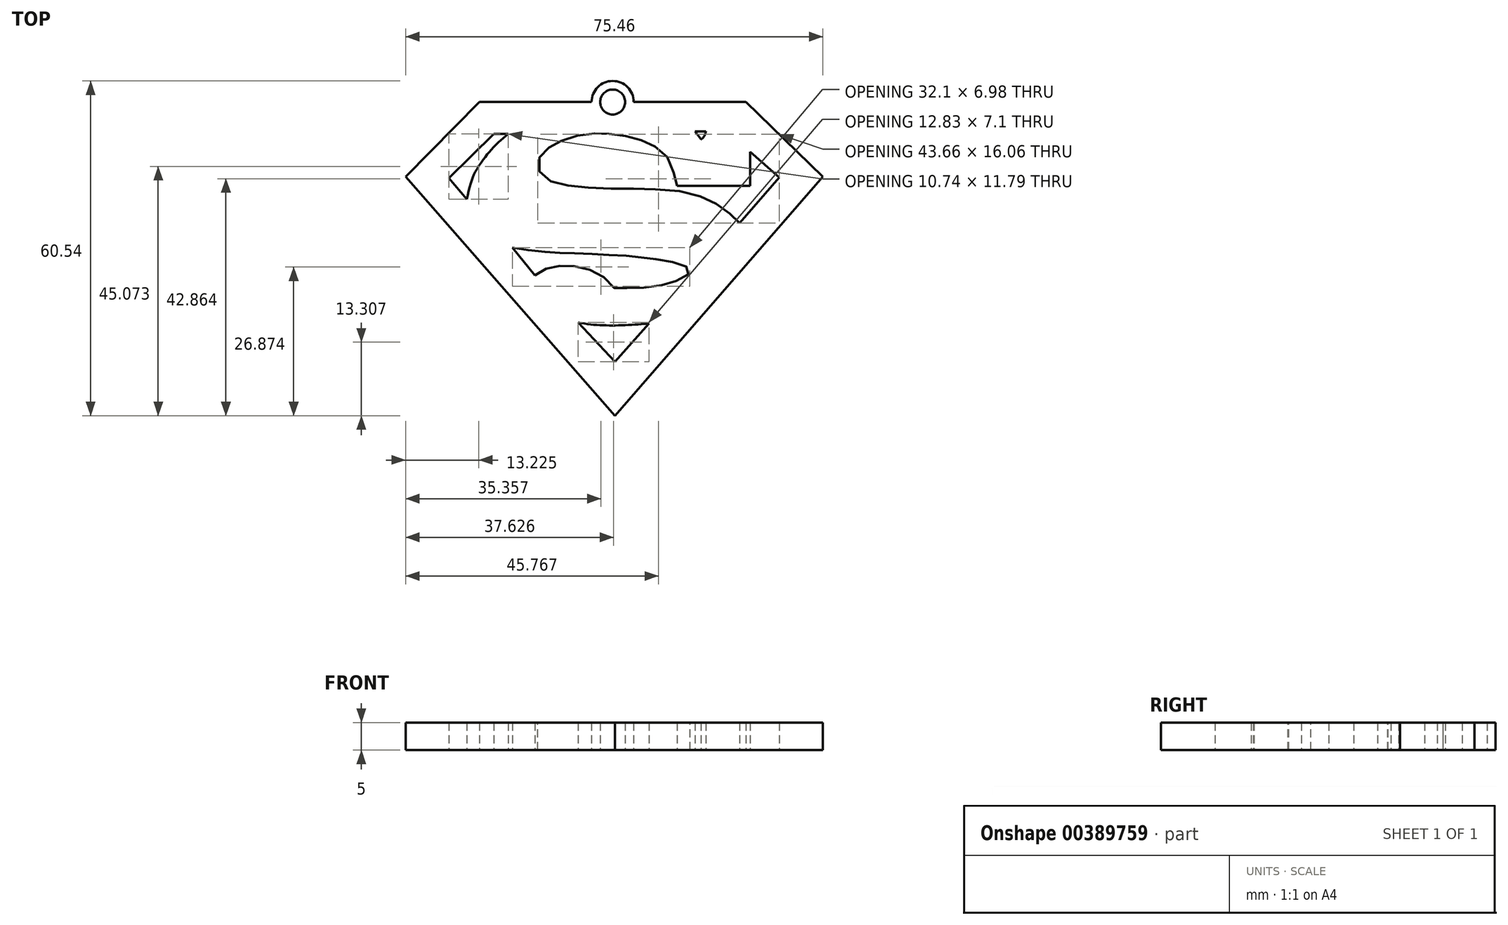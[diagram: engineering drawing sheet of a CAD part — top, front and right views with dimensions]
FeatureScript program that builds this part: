
annotation { "Feature Type Name" : "Feature", "Feature Type Description" : "" }
export const myFeature = defineFeature(function(context is Context, id is Id, definition is map)
    precondition{}
    {
        {
            var Q0;
            Q0=qCreatedBy(makeId("Top.planeOp"),FACE);
            var sketch = newSketch(context, id + "F0", { "sketchPlane" : qUnion([Q0])});
            skLineSegment(sketch, "E0", {"start": v(24.95, 26.24) * mm, "end": v(26.93, 26.24) * mm});
            skLineSegment(sketch, "E1", {"start": v(24.95, 26.24) * mm, "end": v(26.03, 24.83) * mm});
            skFitSpline(sketch, "E2", {"points": [v(26.03, 24.83) * mm, v(26.93, 26.24) * mm], "startDerivative": vector(0.95, 0.22) * mm, "endDerivative": vector(0.66, 2.5) * mm});
            skLineSegment(sketch, "E3", {"start": v(-14.03, 31.56) * mm, "end": v(6.24, 31.56) * mm});
            skLineSegment(sketch, "E4", {"start": v(34.12, 31.56) * mm, "end": v(48.05, 18.07) * mm});
            skLineSegment(sketch, "E5", {"start": v(48.05, 18.07) * mm, "end": v(10.44, -25.17) * mm});
            skLineSegment(sketch, "E6", {"start": v(10.44, -25.17) * mm, "end": v(-27.41, 18.07) * mm});
            skLineSegment(sketch, "E7", {"start": v(-27.41, 18.07) * mm, "end": v(-14.03, 31.56) * mm});
            skLineSegment(sketch, "E8", {"start": v(-19.55, 17.8) * mm, "end": v(-11.43, 25.8) * mm});
            skLineSegment(sketch, "E9", {"start": v(-11.43, 25.8) * mm, "end": v(-8.82, 25.8) * mm});
            skFitSpline(sketch, "E10", {"points": [v(-8.82, 25.8) * mm, v(-10.43, 24.4) * mm, v(-12.07, 22.78) * mm, v(-13.34, 21.14) * mm, v(-14.8, 18.93) * mm, v(-15.57, 16.97) * mm, v(-16.35, 14) * mm], "startDerivative": vector(-10.12, -8.6) * mm, "endDerivative": vector(-4.14, -16.6) * mm});
            skLineSegment(sketch, "E11", {"start": v(-19.55, 17.8) * mm, "end": v(-16.35, 14) * mm});
            skLineSegment(sketch, "E12", {"start": v(34.9, 22.54) * mm, "end": v(40.19, 17.94) * mm});
            skLineSegment(sketch, "E13", {"start": v(40.19, 17.94) * mm, "end": v(33, 9.67) * mm});
            skLineSegment(sketch, "E14", {"start": v(34.9, 22.54) * mm, "end": v(34.9, 16.4) * mm});
            skLineSegment(sketch, "E15", {"start": v(34.9, 16.4) * mm, "end": v(21.72, 16.4) * mm});
            skFitSpline(sketch, "E16", {"points": [v(21.72, 16.4) * mm, v(21.43, 17.55) * mm, v(20.76, 19.79) * mm, v(19.83, 21.67) * mm, v(18.23, 23.18) * mm, v(16.56, 24.14) * mm, v(14.68, 24.84) * mm, v(12.53, 25.39) * mm, v(10.3, 25.7) * mm, v(8.28, 25.87) * mm, v(6.64, 25.87) * mm, v(4.24, 25.61) * mm, v(1.71, 24.9) * mm, v(0, 24.17) * mm, v(-1.36, 23.4) * mm, v(-2.54, 22.47) * mm, v(-3.37, 21) * mm, v(-3.34, 19.37) * mm, v(-2.32, 17.83) * mm, v(-0.27, 16.94) * mm, v(2.35, 16.4) * mm, v(5.84, 16.07) * mm, v(10.23, 15.88) * mm, v(14.3, 15.91) * mm, v(18.23, 15.75) * mm, v(23.06, 15.27) * mm, v(26.33, 14.32) * mm, v(28.54, 13.27) * mm, v(30.59, 11.96) * mm, v(32.07, 10.53) * mm, v(33, 9.67) * mm], "startDerivative": vector(-10.56, 43.93) * mm, "endDerivative": vector(36.17, -32.43) * mm});
            skPoint(sketch, "E17.0.internal.orphan", {"position": v(0, -5.74) * mm});
            skPoint(sketch, "E17.6.internal.orphan", {"position": v(18.38, -5.74) * mm});
            skLineSegment(sketch, "E18", {"start": v(-8.1, 5.2) * mm, "end": v(-4.02, 0.22) * mm});
            skFitSpline(sketch, "E19", {"points": [v(-4.02, 0.22) * mm, v(-2.76, 1.06) * mm, v(-1.03, 1.74) * mm, v(0.76, 1.96) * mm, v(2.55, 1.93) * mm, v(4.92, 1.51) * mm, v(7, 0.71) * mm, v(9.02, -0.63) * mm, v(10.36, -2.07) * mm, v(11.58, -2.1) * mm, v(13.76, -2.07) * mm, v(16.7, -1.91) * mm, v(19.48, -1.47) * mm, v(21.37, -0.89) * mm, v(23.16, 0) * mm, v(24, 0.8) * mm, v(23.8, 1.48) * mm, v(22.59, 2.12) * mm, v(20.44, 2.73) * mm, v(17.92, 3.14) * mm, v(15.93, 3.4) * mm, v(13.47, 3.62) * mm, v(11.8, 3.82) * mm, v(8.57, 3.91) * mm, v(6.04, 4.1) * mm, v(3.2, 4.2) * mm, v(1.18, 4.26) * mm, v(-1.1, 4.33) * mm, v(-2.95, 4.55) * mm, v(-5.9, 4.84) * mm, v(-8.1, 5.2) * mm], "startDerivative": vector(41.85, 30.64) * mm, "endDerivative": vector(-59.82, 10.98) * mm});
            skLineSegment(sketch, "E20", {"start": v(3.8, -8.31) * mm, "end": v(10.45, -15.41) * mm});
            skLineSegment(sketch, "E21", {"start": v(10.45, -15.41) * mm, "end": v(16.63, -8.47) * mm});
            skFitSpline(sketch, "E22", {"points": [v(3.8, -8.31) * mm, v(6, -8.66) * mm, v(8.18, -8.8) * mm, v(10.35, -8.85) * mm, v(12.67, -8.77) * mm, v(15, -8.66) * mm, v(16.63, -8.47) * mm], "startDerivative": vector(12.97, -2.27) * mm, "endDerivative": vector(10.66, 1.46) * mm});
            skPoint(sketch, "E23.center.orphan", {"position": v(10.05, 31.56) * mm});
            skPoint(sketch, "E24.start.orphan", {"position": v(46.48, 18.07) * mm});
            skPoint(sketch, "E25.end.orphan", {"position": v(-25.54, 18.07) * mm});
            skPoint(sketch, "E26.12.internal.orphan", {"position": v(0.29, -6.5) * mm});
            skPoint(sketch, "E27.end.orphan", {"position": v(20.14, -6.5) * mm});
            skPoint(sketch, "E28.2.internal.orphan", {"position": v(0, 5.67) * mm});
            skPoint(sketch, "E29.2.internal.orphan", {"position": v(-2, 0) * mm});
            skPoint(sketch, "E29.7.internal.orphan", {"position": v(5.18, 0) * mm});
            skPoint(sketch, "E30.11.internal.orphan", {"position": v(0, 15.63) * mm});
            skPoint(sketch, "E30.17.internal.orphan", {"position": v(0, 25.68) * mm});
            skArc(sketch, "E31", {"start": v(13.85, 31.56) * mm, "mid": v(10.05, 35.37) * mm, "end": v(6.24, 31.56) * mm});
            skCircle(sketch, "E32", {"center": v(10.05, 31.56) * mm, "radius": 2.26 * mm});
            skLineSegment(sketch, "E33.trimOffspring", {"start": v(13.85, 31.56) * mm, "end": v(34.12, 31.56) * mm});
            skSolve(sketch);
        }
        {
            var Q0;
            Q0 = qSketchRegion(id + "F0", true);
            extrude(context, id + "F1", {"entities" : qUnion([Q0]), "depth" : 5 * mm});
        }
    });
